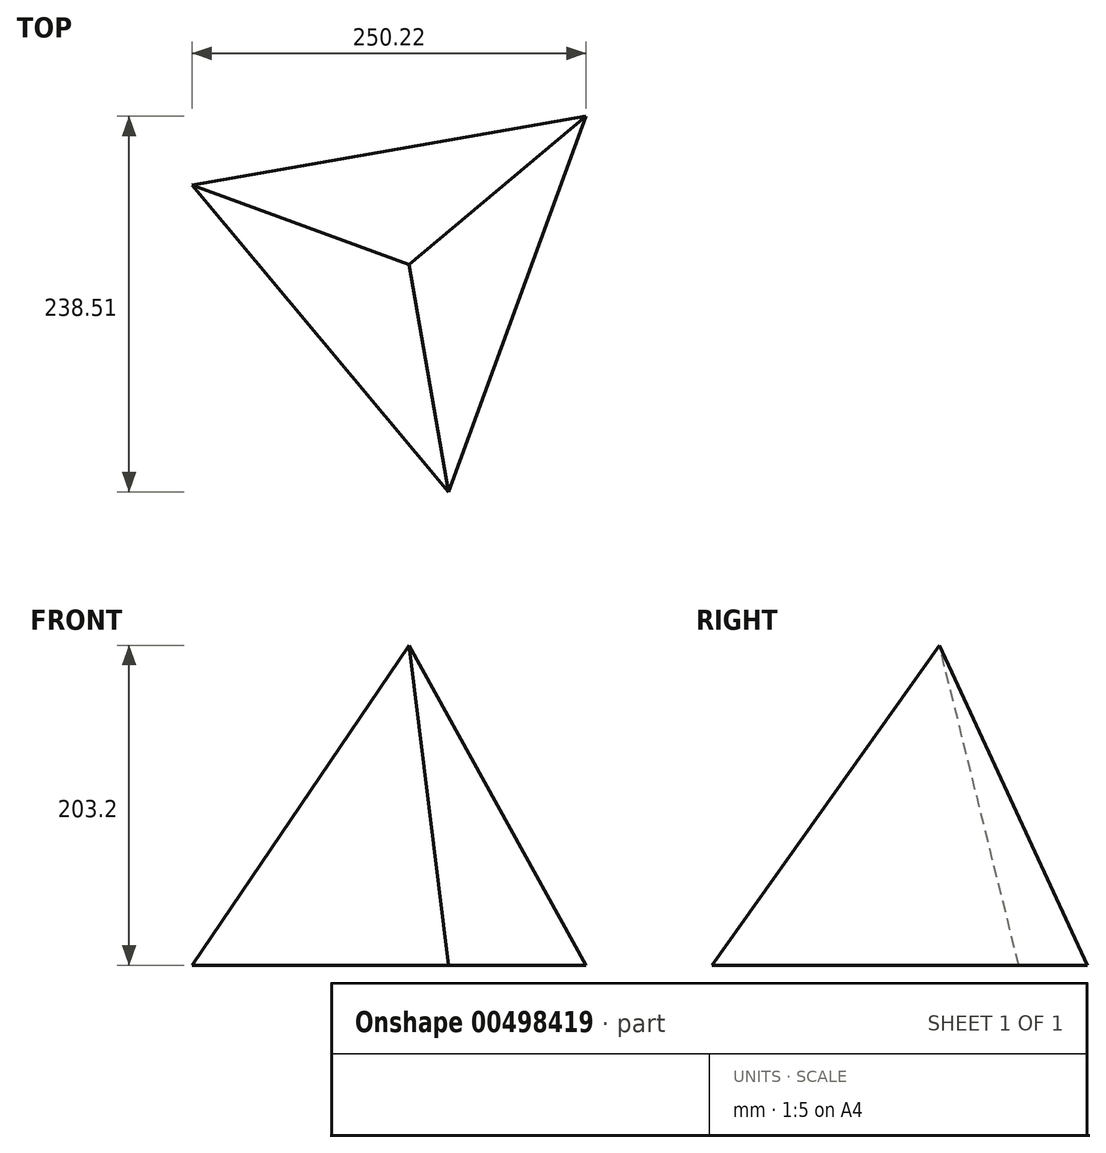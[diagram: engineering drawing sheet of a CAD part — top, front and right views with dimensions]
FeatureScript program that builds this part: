
annotation { "Feature Type Name" : "Feature", "Feature Type Description" : "" }
export const myFeature = defineFeature(function(context is Context, id is Id, definition is map)
    precondition{}
    {
        {
            var Q0;
            Q0=qCreatedBy(makeId("Top.planeOp"),FACE);
            var sketch = newSketch(context, id + "F0", { "sketchPlane" : qUnion([Q0])});
            skCircle(sketch, "E0.cCircle", {"center": v(0, 0) * mm, "radius": 146.65 * mm, "construction": true});
            skLineSegment(sketch, "E0.0", {"start": v(112.52, 94.04) * mm, "end": v(25.18, -144.47) * mm});
            skLineSegment(sketch, "E0.1", {"start": v(25.18, -144.47) * mm, "end": v(-137.7, 50.43) * mm});
            skLineSegment(sketch, "E0.2", {"start": v(-137.7, 50.43) * mm, "end": v(112.52, 94.04) * mm});
            skSolve(sketch);
        }
        {
            var Q0;
            Q0=qCreatedBy(makeId("Top.planeOp"),FACE);
            cPlane(context, id + "F1", {"entities" : qUnion([Q0]), "cplaneType" : CPlaneType.OFFSET, "offset" : 203.2 * mm, "width" : 152.4 * mm, "height" : 152.4 * mm});
        }
        {
            var Q0;
            Q0=qCreatedBy(id+"F1.planeOp",FACE);
            var sketch = newSketch(context, id + "F2", { "sketchPlane" : qUnion([Q0])});
            skPoint(sketch, "E1", {"position": v(0, 0) * mm});
            skSolve(sketch);
        }
        {
            var Q0;
            Q0=makeQuery(id+"F0.imprint","IMPRINT",FACE,{"disambiguationData":[TD([[makeQuery(id+"F0.imprint","IMPRINT",EDGE,{"derivedFrom":sQuery(id+"F0.wireOp",EDGE,"E0.0")}),-1.0]])]});
            var Q1;
            Q1=sQuery(id+"F2.wireOp",VERTEX,"E1");
            loft(context, id + "F3", {"sheetProfilesArray" : [{ "sheetProfileEntities" : qUnion([Q0]) }, { "sheetProfileEntities" : qUnion([Q1]) }]});
        }
    });
